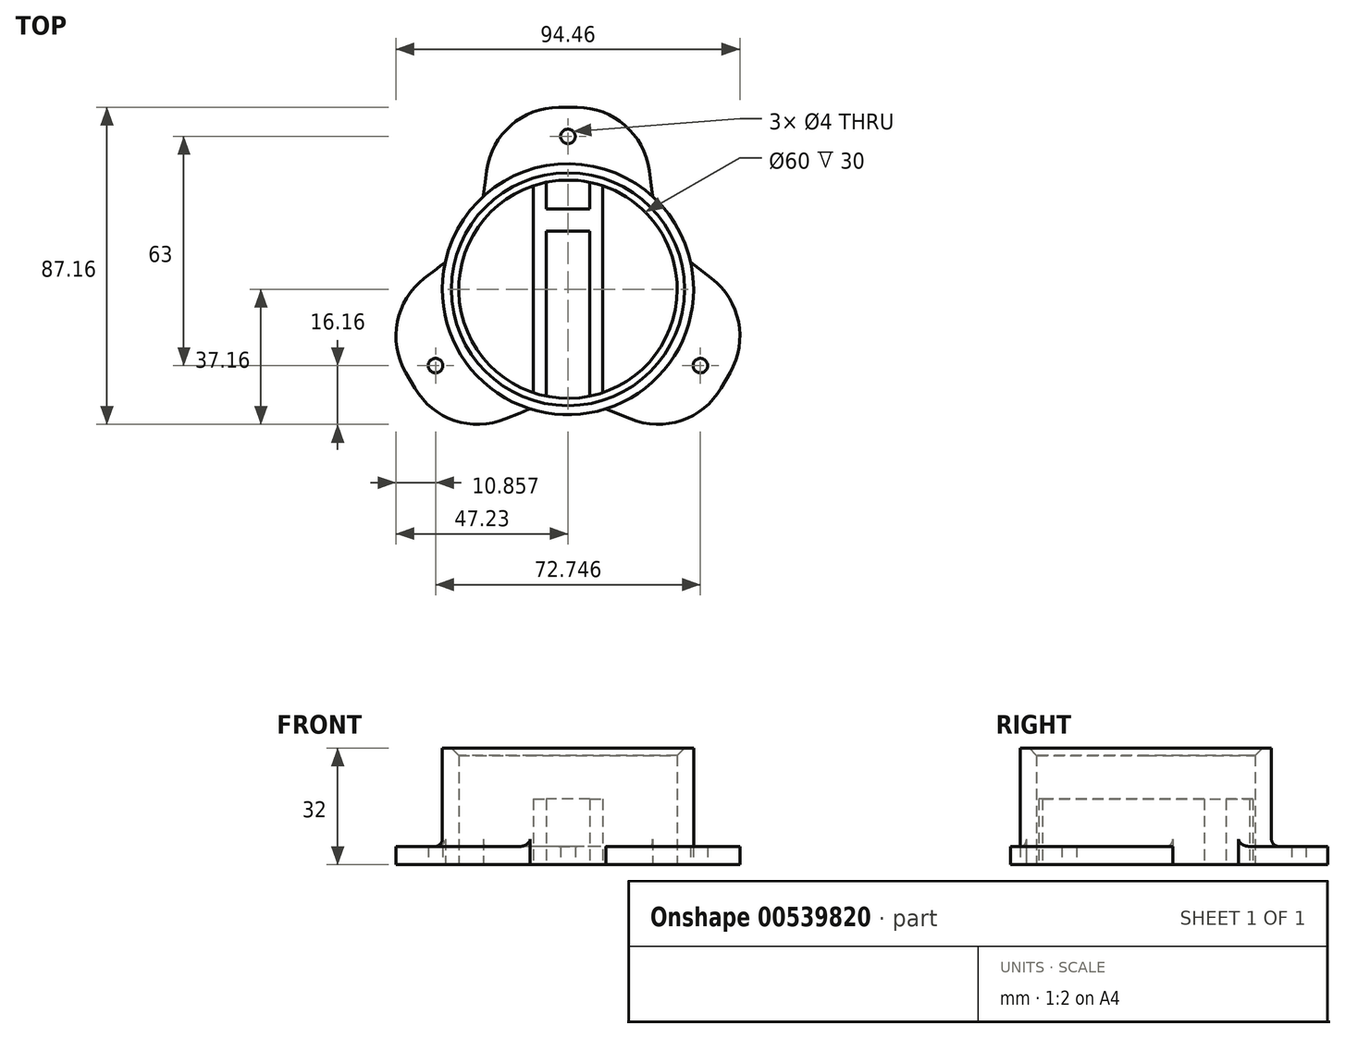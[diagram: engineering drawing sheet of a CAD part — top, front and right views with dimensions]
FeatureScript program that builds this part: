
annotation { "Feature Type Name" : "Feature", "Feature Type Description" : "" }
export const myFeature = defineFeature(function(context is Context, id is Id, definition is map)
    precondition{}
    {
        {
            var Q0;
            Q0=qCreatedBy(makeId("Top.planeOp"),FACE);
            var sketch = newSketch(context, id + "F0", { "sketchPlane" : qUnion([Q0])});
            skLineSegment(sketch, "E0", {"start": v(-2.49, 50) * mm, "end": v(2.49, 50) * mm});
            skLineSegment(sketch, "E1", {"start": v(-22.31, 32.64) * mm, "end": v(-23.27, 25.47) * mm});
            skLineSegment(sketch, "E2", {"start": v(23.27, 25.47) * mm, "end": v(22.31, 32.64) * mm});
            skPoint(sketch, "E3.visualSharp", {"position": v(-20, 50) * mm});
            skArc(sketch, "E3.filletArc", {"start": v(-2.49, 50) * mm, "mid": v(-15.66, 45.05) * mm, "end": v(-22.31, 32.64) * mm});
            skPoint(sketch, "E4.visualSharp", {"position": v(20, 50) * mm});
            skArc(sketch, "E4.filletArc", {"start": v(22.31, 32.64) * mm, "mid": v(15.66, 45.05) * mm, "end": v(2.49, 50) * mm});
            skLineSegment(sketch, "E5.1.0", {"start": v(-17.11, -35.65) * mm, "end": v(-10.42, -32.89) * mm});
            skArc(sketch, "E5.1.2", {"start": v(-42.06, -27.16) * mm, "mid": v(-31.18, -36.09) * mm, "end": v(-17.11, -35.65) * mm});
            skArc(sketch, "E5.1.3", {"start": v(-39.43, 3) * mm, "mid": v(-46.84, -8.96) * mm, "end": v(-44.55, -22.84) * mm});
            skLineSegment(sketch, "E5.1.4", {"start": v(-33.7, 7.42) * mm, "end": v(-39.43, 3) * mm});
            skPoint(sketch, "E5.1.5", {"position": v(-53.3, -7.68) * mm});
            skPoint(sketch, "E5.1.6", {"position": v(-33.3, -42.32) * mm});
            skLineSegment(sketch, "E5.1.7", {"start": v(-42.06, -27.16) * mm, "end": v(-44.55, -22.84) * mm});
            skLineSegment(sketch, "E5.2.0", {"start": v(39.43, 3) * mm, "end": v(33.7, 7.42) * mm});
            skArc(sketch, "E5.2.2", {"start": v(44.55, -22.84) * mm, "mid": v(46.84, -8.96) * mm, "end": v(39.43, 3) * mm});
            skArc(sketch, "E5.2.3", {"start": v(17.11, -35.65) * mm, "mid": v(31.18, -36.09) * mm, "end": v(42.06, -27.16) * mm});
            skLineSegment(sketch, "E5.2.4", {"start": v(10.42, -32.89) * mm, "end": v(17.11, -35.65) * mm});
            skPoint(sketch, "E5.2.5", {"position": v(33.3, -42.32) * mm});
            skPoint(sketch, "E5.2.6", {"position": v(53.3, -7.68) * mm});
            skLineSegment(sketch, "E5.2.7", {"start": v(44.55, -22.84) * mm, "end": v(42.06, -27.16) * mm});
            skPoint(sketch, "E5.center", {"position": v(0, 0) * mm});
            skArc(sketch, "E6", {"start": v(-10.42, -32.89) * mm, "mid": v(0, -34.5) * mm, "end": v(10.42, -32.89) * mm});
            skPoint(sketch, "E7.orphan", {"position": v(-27.37, 12.29) * mm});
            skPoint(sketch, "E8.orphan", {"position": v(-24.32, 17.56) * mm});
            skPoint(sketch, "E9.orphan", {"position": v(-25.98, -15) * mm});
            skPoint(sketch, "E10.orphan", {"position": v(-3.04, -29.85) * mm});
            skPoint(sketch, "E11.orphan", {"position": v(3.04, -29.85) * mm});
            skArc(sketch, "E12.trimOffspring", {"start": v(33.7, 7.42) * mm, "mid": v(29.88, 17.25) * mm, "end": v(23.27, 25.47) * mm});
            skPoint(sketch, "E13.orphan", {"position": v(27.37, 12.29) * mm});
            skPoint(sketch, "E14.orphan", {"position": v(24.32, 17.56) * mm});
            skArc(sketch, "E15.trimOffspring", {"start": v(-23.27, 25.47) * mm, "mid": v(-29.88, 17.25) * mm, "end": v(-33.7, 7.42) * mm});
            skPoint(sketch, "E16.end.orphan", {"position": v(0, 50) * mm});
            skPoint(sketch, "E16.start.orphan", {"position": v(0, 30) * mm});
            skCircle(sketch, "E17", {"center": v(0, 42) * mm, "radius": 2 * mm});
            skCircle(sketch, "E18", {"center": v(36.37, -21) * mm, "radius": 2 * mm});
            skCircle(sketch, "E19", {"center": v(-36.37, -21) * mm, "radius": 2 * mm});
            skCircle(sketch, "E20", {"center": v(0, 0) * mm, "radius": 30 * mm});
            skSolve(sketch);
        }
        {
            var Q0;
            Q0 = qSketchRegion(id + "F0", true);
            extrude(context, id + "F1", {"entities" : qUnion([Q0]), "depth" : 5 * mm, "offsetDistance" : 25 * mm});
        }
        {
            var Q0;
            Q0=makeQuery(id+"F1.opExtrude","CAP_FACE",FACE,{"disambiguationData":[OSD([sQuery(id+"F0.wireOp",EDGE,"E0"),sQuery(id+"F0.wireOp",EDGE,"E1"),sQuery(id+"F0.wireOp",EDGE,"E2"),sQuery(id+"F0.wireOp",EDGE,"E3.filletArc"),sQuery(id+"F0.wireOp",EDGE,"E4.filletArc"),sQuery(id+"F0.wireOp",EDGE,"E5.1.0"),sQuery(id+"F0.wireOp",EDGE,"E5.1.2"),sQuery(id+"F0.wireOp",EDGE,"E5.1.3"),sQuery(id+"F0.wireOp",EDGE,"E5.1.4"),sQuery(id+"F0.wireOp",EDGE,"E5.1.7"),sQuery(id+"F0.wireOp",EDGE,"E5.2.0"),sQuery(id+"F0.wireOp",EDGE,"E5.2.2"),sQuery(id+"F0.wireOp",EDGE,"E5.2.3"),sQuery(id+"F0.wireOp",EDGE,"E5.2.4"),sQuery(id+"F0.wireOp",EDGE,"E5.2.7"),sQuery(id+"F0.wireOp",EDGE,"E6"),sQuery(id+"F0.wireOp",EDGE,"E12.trimOffspring"),sQuery(id+"F0.wireOp",EDGE,"E15.trimOffspring"),sQuery(id+"F0.wireOp",EDGE,"E17"),sQuery(id+"F0.wireOp",EDGE,"E18"),sQuery(id+"F0.wireOp",EDGE,"E19"),sQuery(id+"F0.wireOp",EDGE,"E20")])],"isStart":false});
            var sketch = newSketch(context, id + "F2", { "sketchPlane" : qUnion([Q0])});
            skCircle(sketch, "E21", {"center": v(0, 0) * mm, "radius": 34.5 * mm});
            skCircle(sketch, "E22", {"center": v(0, 0) * mm, "radius": 30 * mm});
            skSolve(sketch);
        }
        {
            var Q0;
            Q0 = qSketchRegion(id + "F2", true);
            extrude(context, id + "F3", {"entities" : qUnion([Q0]), "operationType" : NewBodyOperationType.ADD, "depth" : 27 * mm, "offsetDistance" : 25 * mm});
        }
        {
            var Q0;
            Q0=qCreatedBy(makeId("Top.planeOp"),FACE);
            var sketch = newSketch(context, id + "F4", { "sketchPlane" : qUnion([Q0])});
            skCircle(sketch, "E23", {"center": v(0, 0) * mm, "radius": 30 * mm});
            skLineSegment(sketch, "E24", {"start": v(6, 29.4) * mm, "end": v(6, 22) * mm});
            skLineSegment(sketch, "E25", {"start": v(-6, 29.4) * mm, "end": v(-6, 22) * mm});
            skPoint(sketch, "E26.orphan", {"position": v(0, 30) * mm});
            skLineSegment(sketch, "E27", {"start": v(-9.5, 0) * mm, "end": v(-9.5, -28.46) * mm});
            skLineSegment(sketch, "E28", {"start": v(-9.5, -28.46) * mm, "end": v(-9.5, 28.46) * mm});
            skLineSegment(sketch, "E29", {"start": v(9.5, 0) * mm, "end": v(9.5, -28.46) * mm});
            skLineSegment(sketch, "E30", {"start": v(9.5, 0) * mm, "end": v(9.5, 28.46) * mm});
            skLineSegment(sketch, "E31", {"start": v(0, 22) * mm, "end": v(-6, 22) * mm});
            skLineSegment(sketch, "E32", {"start": v(-6, 22) * mm, "end": v(6, 22) * mm});
            skLineSegment(sketch, "E33", {"start": v(0, 16) * mm, "end": v(-6, 16) * mm});
            skLineSegment(sketch, "E34", {"start": v(-6, 16) * mm, "end": v(6, 16) * mm});
            skLineSegment(sketch, "E35.trimOffspring", {"start": v(6, 16) * mm, "end": v(6, -7) * mm});
            skLineSegment(sketch, "E36.trimOffspring", {"start": v(-6, 16) * mm, "end": v(-6, -7) * mm});
            skLineSegment(sketch, "E37", {"start": v(-3, -7) * mm, "end": v(-6, -7) * mm});
            skLineSegment(sketch, "E38", {"start": v(-6, -7) * mm, "end": v(-3, -7) * mm});
            skLineSegment(sketch, "E39", {"start": v(0, -14) * mm, "end": v(-6, -14) * mm});
            skLineSegment(sketch, "E40", {"start": v(-6, -14) * mm, "end": v(6, -14) * mm});
            skLineSegment(sketch, "E41.trimOffspring", {"start": v(-6, -14) * mm, "end": v(-6, -29.4) * mm});
            skLineSegment(sketch, "E42.trimOffspring", {"start": v(6, -14) * mm, "end": v(6, -29.4) * mm});
            skLineSegment(sketch, "E43", {"start": v(-6, -7) * mm, "end": v(-6, -9) * mm});
            skLineSegment(sketch, "E44", {"start": v(6, -9) * mm, "end": v(6.38, -9) * mm});
            skLineSegment(sketch, "E45", {"start": v(6, -7) * mm, "end": v(6, -14) * mm});
            skLineSegment(sketch, "E46", {"start": v(-6, -7) * mm, "end": v(-6, -14) * mm});
            skLineSegment(sketch, "E47", {"start": v(6, -7) * mm, "end": v(3, -7) * mm});
            skLineSegment(sketch, "E48.trimOffspring", {"start": v(3, -7) * mm, "end": v(6, -7) * mm});
            skPoint(sketch, "E49.orphan", {"position": v(0, -7) * mm});
            skLineSegment(sketch, "E50", {"start": v(-3, -7) * mm, "end": v(-3, -9) * mm});
            skLineSegment(sketch, "E51", {"start": v(3, -7) * mm, "end": v(3, -9) * mm});
            skLineSegment(sketch, "E52", {"start": v(3, -9) * mm, "end": v(-3, -9) * mm});
            skSolve(sketch);
        }
        {
            var Q0;
            {var subQ6=sQuery(id+"F4.wireOp",EDGE,"E24");Q0=makeQuery(id+"F4.imprint","IMPRINT",FACE,{"disambiguationData":[TD([[makeQuery(id+"F4.imprint","IMPRINT",EDGE,{"derivedFrom":subQ6}),1.0]])]});}
            var Q1;
            {var subQ1=sQuery(id+"F4.wireOp",EDGE,"E38");Q1=makeQuery(id+"F4.imprint","IMPRINT",FACE,{"disambiguationData":[TD([[makeQuery(id+"F4.imprint","IMPRINT",EDGE,{"derivedFrom":subQ1}),-1.0]])]});}
            extrude(context, id + "F5", {"entities" : qUnion([Q0, Q1]), "operationType" : NewBodyOperationType.ADD, "depth" : 18 * mm, "offsetDistance" : 25 * mm});
        }
        {
            var Q0;
            Q0=makeQuery(id+"F3.opExtrude","CAP_EDGE",EDGE,{"disambiguationData":[OSD([sQuery(id+"F2.wireOp",EDGE,"E22")])],"isStart":false});
            chamfer(context, id + "F6", {"entities" : qUnion([Q0]), "width" : 2 * mm, "tangentPropagation" : true});
        }
        {
            var Q0;
            {var subQ2=sQuery(id+"F0.wireOp",EDGE,"E5.1.0");var subQ5=sQuery(id+"F2.wireOp",EDGE,"E21");Q0=makeQuery(id+"F3.boolean.opBoolean","SPLIT",EDGE,{"disambiguationData":[TD([makeQuery(id+"F1.opExtrude","SWEPT_FACE",FACE,{"disambiguationData":[OSD([subQ2])]})])],"derivedFrom":makeQuery(id+"F3.opExtrude","CAP_EDGE",EDGE,{"disambiguationData":[OSD([subQ5])],"isStart":true})});}
            var Q1;
            {var subQ1=sQuery(id+"F0.wireOp",EDGE,"E1");var subQ5=sQuery(id+"F2.wireOp",EDGE,"E21");Q1=makeQuery(id+"F3.boolean.opBoolean","SPLIT",EDGE,{"disambiguationData":[TD([makeQuery(id+"F1.opExtrude","SWEPT_FACE",FACE,{"disambiguationData":[OSD([subQ1])]})])],"derivedFrom":makeQuery(id+"F3.opExtrude","CAP_EDGE",EDGE,{"disambiguationData":[OSD([subQ5])],"isStart":true})});}
            var Q2;
            {var subQ2=sQuery(id+"F0.wireOp",EDGE,"E5.2.0");var subQ3=sQuery(id+"F2.wireOp",EDGE,"E21");Q2=makeQuery(id+"F3.boolean.opBoolean","SPLIT",EDGE,{"disambiguationData":[TD([makeQuery(id+"F1.opExtrude","SWEPT_FACE",FACE,{"disambiguationData":[OSD([subQ2])]})])],"derivedFrom":makeQuery(id+"F3.opExtrude","CAP_EDGE",EDGE,{"disambiguationData":[OSD([subQ3])],"isStart":true})});}
            fillet(context, id + "F7", {"entities" : qUnion([Q0, Q1, Q2]), "radius" : 2 * mm, "tangentPropagation" : true, "allowEdgeOverflow" : false});
        }
        {
            var Q0;
            Q0=makeQuery(id+"F5.boolean.opBoolean","MERGE",FACE,{"derivedFrom":[makeQuery(id+"F1.opExtrude","CAP_FACE",FACE,{"disambiguationData":[OSD([sQuery(id+"F0.wireOp",EDGE,"E0"),sQuery(id+"F0.wireOp",EDGE,"E1"),sQuery(id+"F0.wireOp",EDGE,"E2"),sQuery(id+"F0.wireOp",EDGE,"E3.filletArc"),sQuery(id+"F0.wireOp",EDGE,"E4.filletArc"),sQuery(id+"F0.wireOp",EDGE,"E5.1.0"),sQuery(id+"F0.wireOp",EDGE,"E5.1.2"),sQuery(id+"F0.wireOp",EDGE,"E5.1.3"),sQuery(id+"F0.wireOp",EDGE,"E5.1.4"),sQuery(id+"F0.wireOp",EDGE,"E5.1.7"),sQuery(id+"F0.wireOp",EDGE,"E5.2.0"),sQuery(id+"F0.wireOp",EDGE,"E5.2.2"),sQuery(id+"F0.wireOp",EDGE,"E5.2.3"),sQuery(id+"F0.wireOp",EDGE,"E5.2.4"),sQuery(id+"F0.wireOp",EDGE,"E5.2.7"),sQuery(id+"F0.wireOp",EDGE,"E6"),sQuery(id+"F0.wireOp",EDGE,"E12.trimOffspring"),sQuery(id+"F0.wireOp",EDGE,"E15.trimOffspring"),sQuery(id+"F0.wireOp",EDGE,"E17"),sQuery(id+"F0.wireOp",EDGE,"E18"),sQuery(id+"F0.wireOp",EDGE,"E19"),sQuery(id+"F0.wireOp",EDGE,"E20")])],"isStart":true}),makeQuery(id+"F5.opExtrude","CAP_FACE",FACE,{"disambiguationData":[OSD([sQuery(id+"F4.wireOp",EDGE,"E23"),sQuery(id+"F4.wireOp",EDGE,"E24"),sQuery(id+"F4.wireOp",EDGE,"E25"),sQuery(id+"F4.wireOp",EDGE,"E28"),sQuery(id+"F4.wireOp",EDGE,"E29"),sQuery(id+"F4.wireOp",EDGE,"E30"),sQuery(id+"F4.wireOp",EDGE,"E32"),sQuery(id+"F4.wireOp",EDGE,"E34"),sQuery(id+"F4.wireOp",EDGE,"E35.trimOffspring"),sQuery(id+"F4.wireOp",EDGE,"E36.trimOffspring"),sQuery(id+"F4.wireOp",EDGE,"E40"),sQuery(id+"F4.wireOp",EDGE,"E41.trimOffspring"),sQuery(id+"F4.wireOp",EDGE,"E42.trimOffspring"),sQuery(id+"F4.wireOp",EDGE,"E38"),sQuery(id+"F4.wireOp",EDGE,"E48.trimOffspring"),sQuery(id+"F4.wireOp",EDGE,"E50"),sQuery(id+"F4.wireOp",EDGE,"E51"),sQuery(id+"F4.wireOp",EDGE,"E52")])],"isStart":true})]});
            var sketch = newSketch(context, id + "F8", { "sketchPlane" : qUnion([Q0])});
            skLineSegment(sketch, "E53", {"start": v(-3, 9) * mm, "end": v(-3, 14) * mm});
            skLineSegment(sketch, "E54", {"start": v(3, 9) * mm, "end": v(3, 14) * mm});
            skLineSegment(sketch, "E55", {"start": v(-3, 14) * mm, "end": v(3, 14) * mm});
            skLineSegment(sketch, "E56", {"start": v(-3, 9) * mm, "end": v(3, 9) * mm});
            skSolve(sketch);
        }
        {
            var Q0;
            Q0 = qSketchRegion(id + "F8", true);
            extrude(context, id + "F9", {"entities" : qUnion([Q0]), "operationType" : NewBodyOperationType.REMOVE, "oppositeDirection" : true, "depth" : 10 * mm, "offsetDistance" : 25 * mm});
        }
    });
